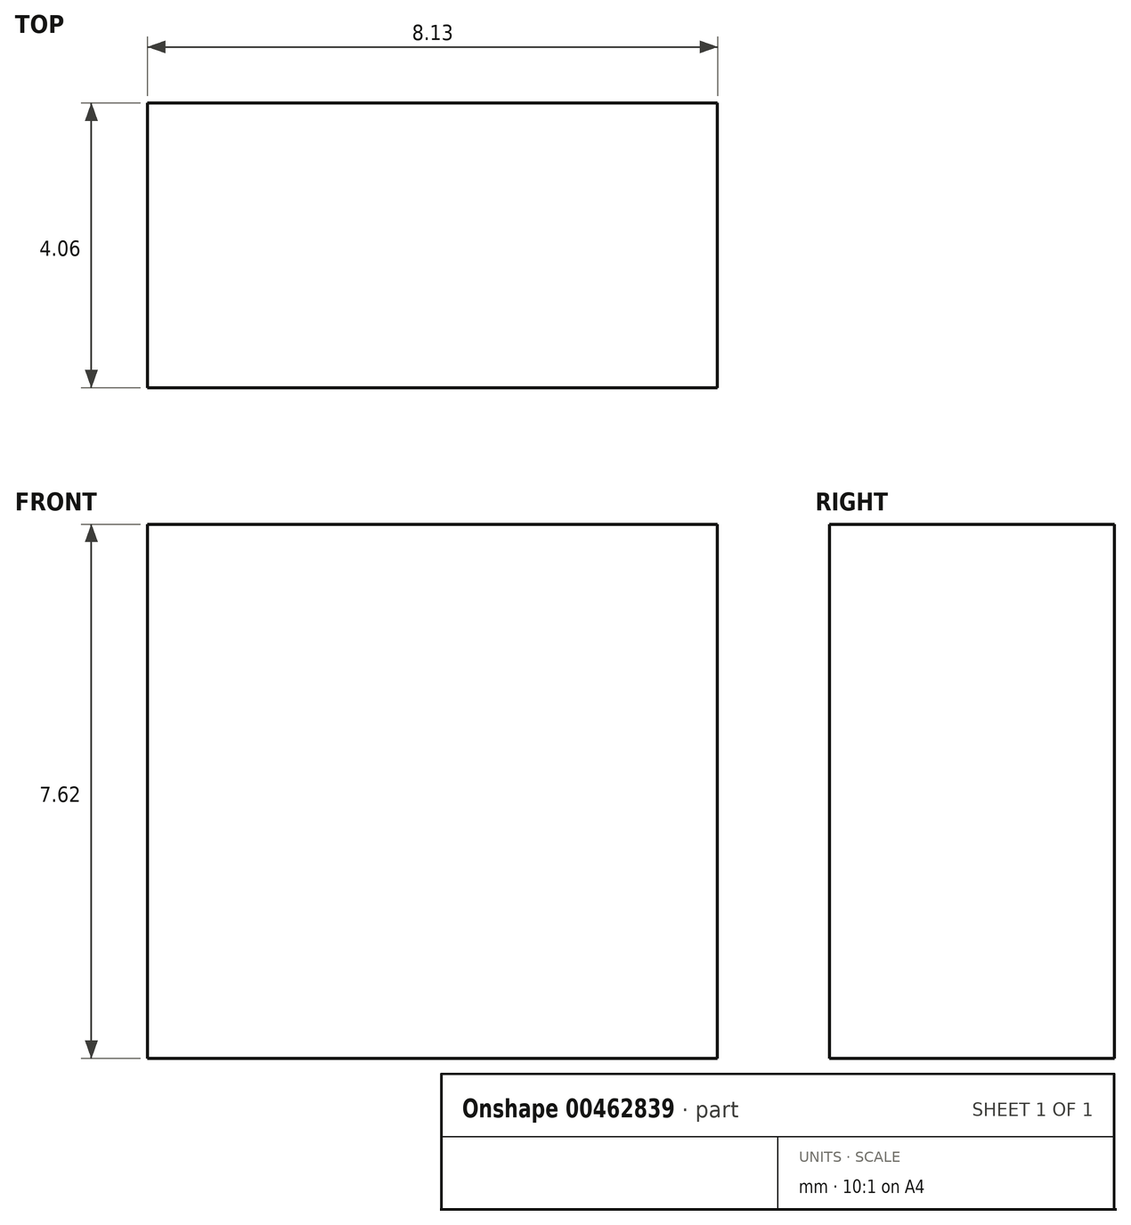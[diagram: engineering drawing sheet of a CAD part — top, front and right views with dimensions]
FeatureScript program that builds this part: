
annotation { "Feature Type Name" : "Feature", "Feature Type Description" : "" }
export const myFeature = defineFeature(function(context is Context, id is Id, definition is map)
    precondition{}
    {
        {
            var Q0;
            Q0=qCreatedBy(makeId("Front.planeOp"),FACE);
            var sketch = newSketch(context, id + "F0", { "sketchPlane" : qUnion([Q0])});
            skLineSegment(sketch, "E0.bottom", {"start": v(-5.97, 3.24) * mm, "end": v(2.16, 3.24) * mm});
            skLineSegment(sketch, "E0.top", {"start": v(-5.97, -4.38) * mm, "end": v(2.16, -4.38) * mm});
            skLineSegment(sketch, "E0.left", {"start": v(-5.97, 3.24) * mm, "end": v(-5.97, -4.38) * mm});
            skLineSegment(sketch, "E0.right", {"start": v(2.16, 3.24) * mm, "end": v(2.16, -4.38) * mm});
            skSolve(sketch);
        }
        {
            var Q0;
            Q0=makeQuery(id+"F0.imprint","IMPRINT",FACE,{"disambiguationData":[TD([[makeQuery(id+"F0.imprint","IMPRINT",EDGE,{"derivedFrom":sQuery(id+"F0.wireOp",EDGE,"E0.bottom")}),-1.0]])]});
            extrude(context, id + "F1", {"entities" : qUnion([Q0]), "depth" : 4.06 * mm});
        }
    });
